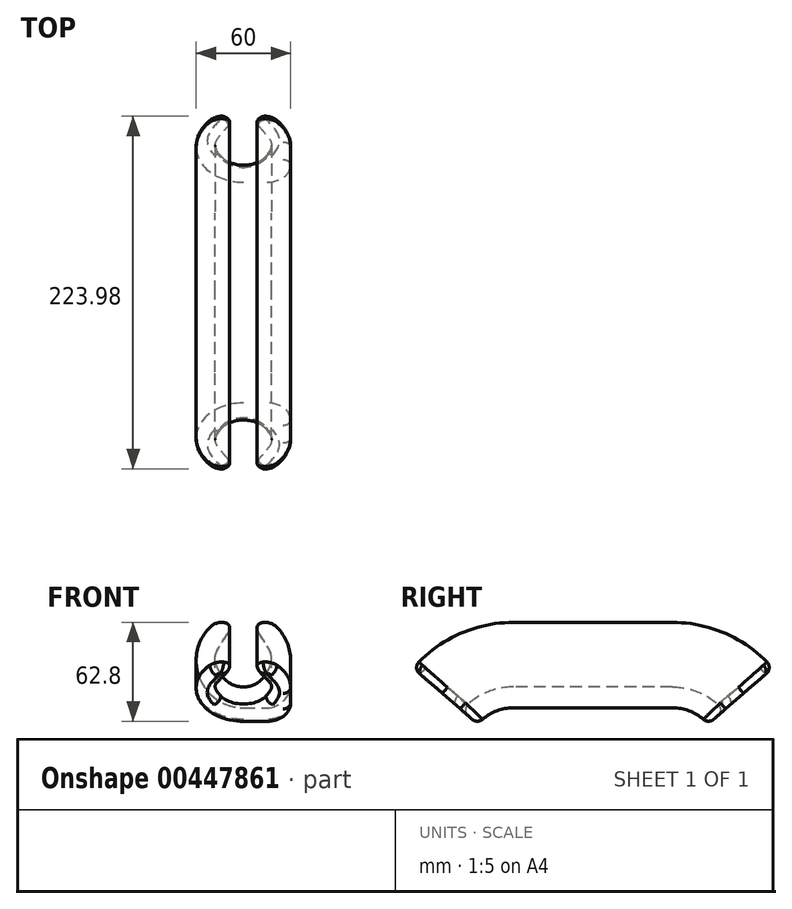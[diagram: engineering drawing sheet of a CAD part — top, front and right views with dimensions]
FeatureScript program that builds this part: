
annotation { "Feature Type Name" : "Feature", "Feature Type Description" : "" }
export const myFeature = defineFeature(function(context is Context, id is Id, definition is map)
    precondition{}
    {
        {
            var Q0;
            Q0=qCreatedBy(makeId("Front.planeOp"),FACE);
            var sketch = newSketch(context, id + "F0", { "sketchPlane" : qUnion([Q0])});
            skArc(sketch, "E0", {"start": v(30, 0) * mm, "mid": v(27.72, 11.48) * mm, "end": v(21.21, 21.21) * mm});
            skLineSegment(sketch, "E1", {"start": v(30, 0) * mm, "end": v(30, -15) * mm});
            skLineSegment(sketch, "E2", {"start": v(0, -30) * mm, "end": v(15, -30) * mm});
            skPoint(sketch, "E3", {"position": v(30, -15) * mm});
            skPoint(sketch, "E4", {"position": v(15, -30) * mm});
            skArc(sketch, "E5", {"start": v(15, -30) * mm, "mid": v(25.6, -25.6) * mm, "end": v(30, -15) * mm});
            skPoint(sketch, "E6.orphan", {"position": v(30, -30) * mm});
            skPoint(sketch, "E7", {"position": v(0, 30) * mm});
            skPoint(sketch, "E8", {"position": v(21.21, 21.21) * mm});
            skArc(sketch, "E9", {"start": v(0, -16.7) * mm, "mid": v(8.3, -14.5) * mm, "end": v(14.4, -8.46) * mm});
            skFitSpline(sketch, "E10", {"points": [v(14.4, -8.46) * mm, v(17.38, 4.69) * mm, v(8.88, 21.94) * mm, v(21.21, 21.21) * mm], "startDerivative": vector(21.5, 36.57) * mm, "endDerivative": vector(41.98, -41.98) * mm});
            skPoint(sketch, "E11", {"position": v(0, -16.7) * mm});
            skFitSpline(sketch, "E12.MirrorCS", {"points": [v(-14.4, -8.46) * mm, v(-17.38, 4.69) * mm, v(-8.88, 21.94) * mm, v(-21.21, 21.21) * mm], "startDerivative": vector(-21.5, 36.57) * mm, "endDerivative": vector(-41.98, -41.98) * mm});
            skArc(sketch, "E13.MirrorCS", {"start": v(0, -16.7) * mm, "mid": v(-8.3, -14.5) * mm, "end": v(-14.4, -8.46) * mm});
            skArc(sketch, "E14.trimOffspring", {"start": v(-21.21, 21.21) * mm, "mid": v(-27.72, -11.48) * mm, "end": v(0, -30) * mm});
            skSolve(sketch);
        }
        {
            var Q0;
            Q0=qCreatedBy(makeId("Right.planeOp"),FACE);
            var sketch = newSketch(context, id + "F1", { "sketchPlane" : qUnion([Q0])});
            skLineSegment(sketch, "E15", {"start": v(0, 0) * mm, "end": v(-50.5, 0) * mm});
            skArc(sketch, "E16", {"start": v(-50.5, 0) * mm, "mid": v(-75.4, -5.41) * mm, "end": v(-95.82, -20.68) * mm});
            skSolve(sketch);
        }
        {
            var Q0;
            Q0=makeQuery(id+"F0.imprint","IMPRINT",FACE,{"disambiguationData":[TD([[makeQuery(id+"F0.imprint","IMPRINT",EDGE,{"derivedFrom":sQuery(id+"F0.wireOp",EDGE,"E0")}),1.0]])]});
            var Q1;
            Q1=sQuery(id+"F1.wireOp",EDGE,"E16");
            var Q2;
            Q2=sQuery(id+"F1.wireOp",EDGE,"E15");
            sweep(context, id + "F2", {"profiles" : qUnion([Q0]), "path" : qUnion([Q1, Q2])});
        }
        {
            var Q0;
            Q0=makeQuery(id+"F2.opSweep","SWEPT_BODY",BODY,{"disambiguationData":[OSD([sQuery(id+"F0.wireOp",EDGE,"E0"),sQuery(id+"F0.wireOp",EDGE,"E1"),sQuery(id+"F0.wireOp",EDGE,"E2"),sQuery(id+"F0.wireOp",EDGE,"E5"),sQuery(id+"F0.wireOp",EDGE,"E9"),sQuery(id+"F0.wireOp",EDGE,"E10"),sQuery(id+"F0.wireOp",EDGE,"E12.MirrorCS"),sQuery(id+"F0.wireOp",EDGE,"E13.MirrorCS"),sQuery(id+"F0.wireOp",EDGE,"E14.trimOffspring"),sQuery(id+"F1.wireOp",EDGE,"E15")])]});
            var Q1;
            Q1=qCreatedBy(makeId("Front.planeOp"),FACE);
            mirror(context, id + "F3", {"operationType" : NewBodyOperationType.ADD, "entities" : qUnion([Q0]), "mirrorPlane" : qUnion([Q1])});
        }
        {
            var Q0;
            Q0=makeQuery(id+"F2.opSweep","CAP_FACE",FACE,{"disambiguationData":[OSD([sQuery(id+"F0.wireOp",EDGE,"E0"),sQuery(id+"F0.wireOp",EDGE,"E1"),sQuery(id+"F0.wireOp",EDGE,"E2"),sQuery(id+"F0.wireOp",EDGE,"E5"),sQuery(id+"F0.wireOp",EDGE,"E9"),sQuery(id+"F0.wireOp",EDGE,"E10"),sQuery(id+"F0.wireOp",EDGE,"E12.MirrorCS"),sQuery(id+"F0.wireOp",EDGE,"E13.MirrorCS"),sQuery(id+"F0.wireOp",EDGE,"E14.trimOffspring"),sQuery(id+"F1.wireOp",VERTEX,"E16.end")])],"isStart":false});
            var Q1;
            Q1=makeQuery(id+"F3.opPattern","COPY",FACE,{"derivedFrom":makeQuery(id+"F2.opSweep","CAP_FACE",FACE,{"disambiguationData":[OSD([sQuery(id+"F0.wireOp",EDGE,"E0"),sQuery(id+"F0.wireOp",EDGE,"E1"),sQuery(id+"F0.wireOp",EDGE,"E2"),sQuery(id+"F0.wireOp",EDGE,"E5"),sQuery(id+"F0.wireOp",EDGE,"E9"),sQuery(id+"F0.wireOp",EDGE,"E10"),sQuery(id+"F0.wireOp",EDGE,"E12.MirrorCS"),sQuery(id+"F0.wireOp",EDGE,"E13.MirrorCS"),sQuery(id+"F0.wireOp",EDGE,"E14.trimOffspring"),sQuery(id+"F1.wireOp",VERTEX,"E16.end")])],"isStart":false}),"instanceName":"1"});
            fillet(context, id + "F4", {"entities" : qUnion([Q0, Q1]), "radius" : 5 * mm, "tangentPropagation" : true, "allowEdgeOverflow" : false});
        }
    });
